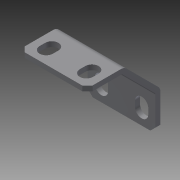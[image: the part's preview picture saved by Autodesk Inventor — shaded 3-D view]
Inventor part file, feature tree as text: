
AUTODESK INVENTOR PART (.ipt)
format: ipt  version: 2015 (Build 190159000, 159)  size: 131,584 bytes
history: native  units: in
note: dims shown in document units (in); Inventor stores cm internally (conversion verified against a paired STEP export)
features: other x1, chamfer x1, imported_body x1
ambient origin geometry x8: Origin, YZ Plane, XZ Plane, XY Plane, X Axis, Y Axis, Z Axis, Center Point
bodies: Body1 (feature_tree)
feature tree (3):
  other  "Right-Angle Corner Gusset"
  chamfer  "Chamfer1"  [1 undecoded]
  imported_body  "Base1"
note: 1 required parameter value undecoded (feature->parameter linkage not recoverable at this tier; creation-order binding heuristic only, values carry confidence <= 0.55)
